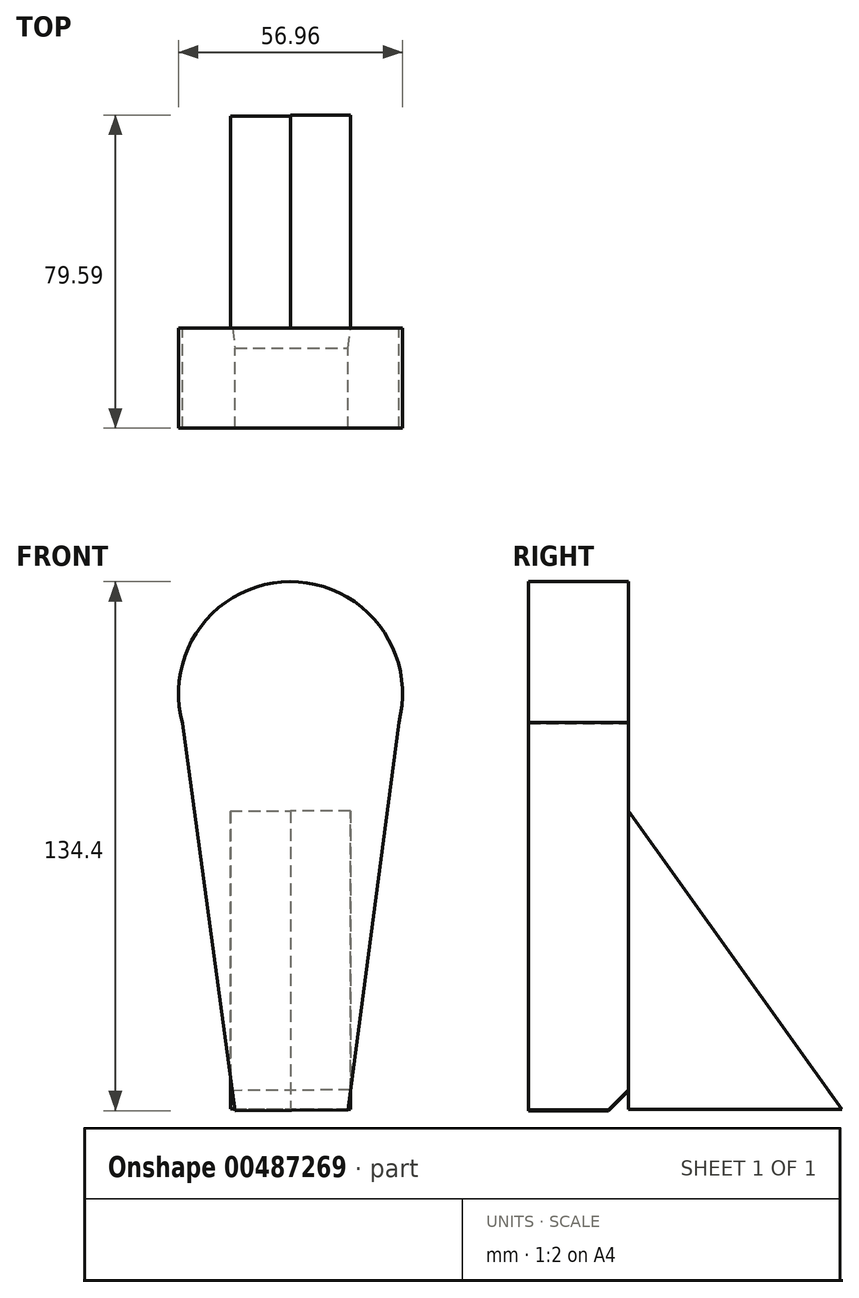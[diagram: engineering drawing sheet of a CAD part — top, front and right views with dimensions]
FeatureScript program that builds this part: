
annotation { "Feature Type Name" : "Feature", "Feature Type Description" : "" }
export const myFeature = defineFeature(function(context is Context, id is Id, definition is map)
    precondition{}
    {
        {
            var Q0;
            Q0=qCreatedBy(makeId("Front.planeOp"),FACE);
            var sketch = newSketch(context, id + "F0", { "sketchPlane" : qUnion([Q0])});
            skCircle(sketch, "E0", {"center": v(0, 29.77) * mm, "radius": 28.48 * mm});
            skLineSegment(sketch, "E1", {"start": v(-28.48, 29.77) * mm, "end": v(-14.07, -76.15) * mm});
            skLineSegment(sketch, "E2", {"start": v(28.48, 29.77) * mm, "end": v(14.62, -75.97) * mm});
            skLineSegment(sketch, "E3", {"start": v(14.62, -75.97) * mm, "end": v(-14.07, -76.15) * mm});
            skSolve(sketch);
        }
        {
            var Q0;
            Q0 = qSketchRegion(id + "F0", true);
            extrude(context, id + "F1", {"entities" : qUnion([Q0]), "depth" : 25.4 * mm});
        }
        {
            var Q0;
            Q0=makeQuery(id+"F1.opExtrude","CAP_EDGE",EDGE,{"disambiguationData":[OSD([sQuery(id+"F0.wireOp",EDGE,"E3")])],"isStart":true});
            chamfer(context, id + "F2", {"entities" : qUnion([Q0]), "width" : 5.08 * mm, "tangentPropagation" : true});
        }
        {
            var Q0;
            Q0=qCreatedBy(makeId("Right.planeOp"),FACE);
            var sketch = newSketch(context, id + "F3", { "sketchPlane" : qUnion([Q0])});
            skLineSegment(sketch, "E4", {"start": v(0, 0) * mm, "end": v(54.2, -75.84) * mm});
            skLineSegment(sketch, "E5", {"start": v(54.2, -75.84) * mm, "end": v(0, -75.84) * mm});
            skLineSegment(sketch, "E6", {"start": v(0, -75.84) * mm, "end": v(0, 0) * mm});
            skSolve(sketch);
        }
        {
            var Q0;
            Q0=makeQuery(id+"F3.imprint","IMPRINT",FACE,{"disambiguationData":[TD([[makeQuery(id+"F3.imprint","IMPRINT",EDGE,{"derivedFrom":sQuery(id+"F3.wireOp",EDGE,"E4")}),-1.0]])]});
            extrude(context, id + "F4", {"entities" : qUnion([Q0]), "operationType" : NewBodyOperationType.ADD, "depth" : 15.24 * mm});
        }
        {
            var Q0;
            Q0=qCreatedBy(makeId("Right.planeOp"),FACE);
            var sketch = newSketch(context, id + "F5", { "sketchPlane" : qUnion([Q0])});
            skLineSegment(sketch, "E7", {"start": v(0, 0) * mm, "end": v(53.83, -75.63) * mm});
            skLineSegment(sketch, "E8", {"start": v(53.83, -75.63) * mm, "end": v(0, -75.63) * mm});
            skLineSegment(sketch, "E9", {"start": v(0, -75.63) * mm, "end": v(0, 0) * mm});
            skSolve(sketch);
        }
        {
            var Q0;
            Q0 = qSketchRegion(id + "F5", true);
            extrude(context, id + "F6", {"entities" : qUnion([Q0]), "operationType" : NewBodyOperationType.ADD, "oppositeDirection" : true, "depth" : 15.24 * mm});
        }
    });
